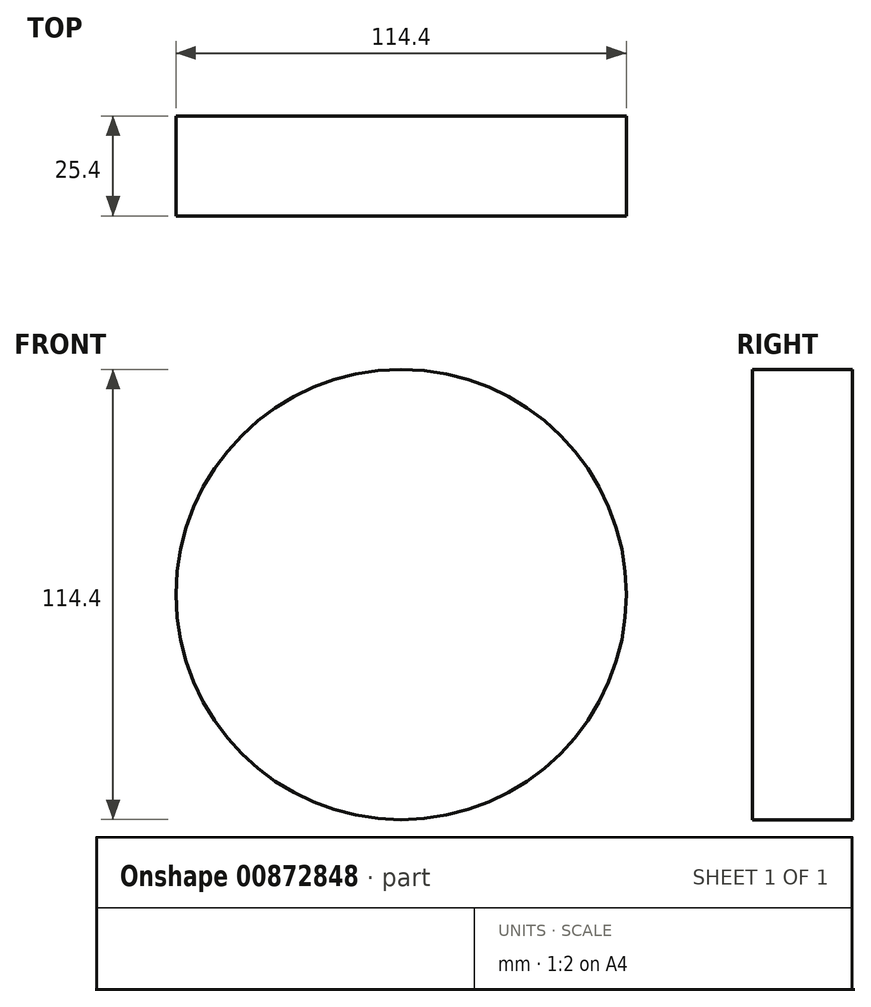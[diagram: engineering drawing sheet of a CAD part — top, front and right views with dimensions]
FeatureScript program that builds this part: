
annotation { "Feature Type Name" : "Feature", "Feature Type Description" : "" }
export const myFeature = defineFeature(function(context is Context, id is Id, definition is map)
    precondition{}
    {
        {
            var Q0;
            Q0=qCreatedBy(makeId("Front.planeOp"),FACE);
            var sketch = newSketch(context, id + "F0", { "sketchPlane" : qUnion([Q0])});
            skCircle(sketch, "E0", {"center": v(0, 0) * mm, "radius": 57.2 * mm});
            skSolve(sketch);
        }
        {
            var Q0;
            Q0 = qSketchRegion(id + "F0", true);
            extrude(context, id + "F1", {"entities" : qUnion([Q0]), "depth" : 25.4 * mm, "offsetDistance" : 25.4 * mm});
        }
    });
